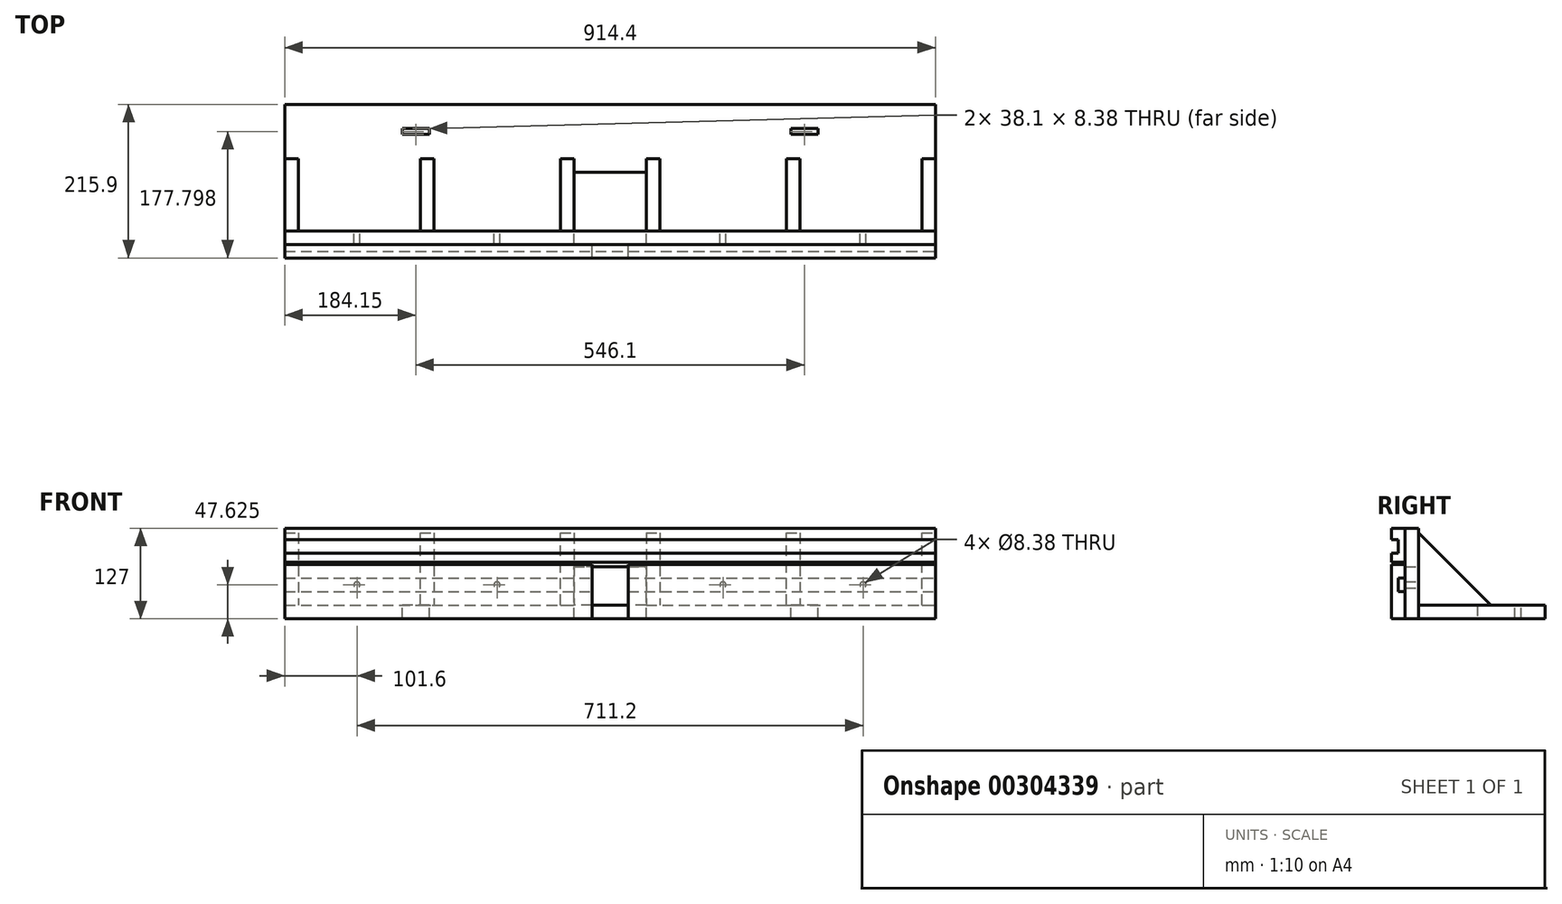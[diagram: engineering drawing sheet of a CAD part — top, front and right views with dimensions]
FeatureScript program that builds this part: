
annotation { "Feature Type Name" : "Feature", "Feature Type Description" : "" }
export const myFeature = defineFeature(function(context is Context, id is Id, definition is map)
    precondition{}
    {
        {
            var Q0;
            Q0=qCreatedBy(makeId("Top.planeOp"),FACE);
            var sketch = newSketch(context, id + "F0", { "sketchPlane" : qUnion([Q0])});
            skLineSegment(sketch, "E0.bottom", {"start": v(-457.2, 69.56) * mm, "end": v(457.2, 69.56) * mm});
            skLineSegment(sketch, "E0.top", {"start": v(-457.2, -108.24) * mm, "end": v(457.2, -108.24) * mm});
            skLineSegment(sketch, "E0.left", {"start": v(-457.2, 69.56) * mm, "end": v(-457.2, -108.24) * mm});
            skLineSegment(sketch, "E0.right", {"start": v(457.2, 69.56) * mm, "end": v(457.2, -108.24) * mm});
            skPoint(sketch, "E1", {"position": v(0, 69.56) * mm});
            skSolve(sketch);
        }
        {
            var Q0;
            Q0=makeQuery(id+"F0.imprint","IMPRINT",FACE,{"disambiguationData":[TD([[makeQuery(id+"F0.imprint","IMPRINT",EDGE,{"derivedFrom":sQuery(id+"F0.wireOp",EDGE,"E0.bottom")}),-1.0]])]});
            extrude(context, id + "F1", {"entities" : qUnion([Q0]), "depth" : 19.05 * mm});
        }
        {
            var Q0;
            Q0=makeQuery(id+"F1.opExtrude","CAP_FACE",FACE,{"disambiguationData":[OSD([sQuery(id+"F0.wireOp",EDGE,"E0.bottom"),sQuery(id+"F0.wireOp",EDGE,"E0.top"),sQuery(id+"F0.wireOp",EDGE,"E0.left"),sQuery(id+"F0.wireOp",EDGE,"E0.right")])],"isStart":true});
            var sketch = newSketch(context, id + "F2", { "sketchPlane" : qUnion([Q0])});
            skLineSegment(sketch, "E2.bottom", {"start": v(-457.2, 108.24) * mm, "end": v(457.2, 108.24) * mm});
            skLineSegment(sketch, "E2.top", {"start": v(-457.2, 127.3) * mm, "end": v(457.2, 127.3) * mm});
            skLineSegment(sketch, "E2.left", {"start": v(-457.2, 108.24) * mm, "end": v(-457.2, 127.3) * mm});
            skLineSegment(sketch, "E2.right", {"start": v(457.2, 108.24) * mm, "end": v(457.2, 127.3) * mm});
            skSolve(sketch);
        }
        {
            var Q0;
            Q0=makeQuery(id+"F2.imprint","IMPRINT",FACE,{"disambiguationData":[TD([[makeQuery(id+"F2.imprint","IMPRINT",EDGE,{"derivedFrom":sQuery(id+"F2.wireOp",EDGE,"E2.bottom")}),1.0]])]});
            extrude(context, id + "F3", {"entities" : qUnion([Q0]), "oppositeDirection" : true, "depth" : 127 * mm});
        }
        {
            var Q0;
            Q0=makeQuery(id+"F3.opExtrude","SWEPT_FACE",FACE,{"disambiguationData":[OSD([sQuery(id+"F2.wireOp",EDGE,"E2.top")])]});
            var sketch = newSketch(context, id + "F4", { "sketchPlane" : qUnion([Q0])});
            skLineSegment(sketch, "E3.bottom", {"start": v(-457.2, 0) * mm, "end": v(-25.4, 0) * mm});
            skLineSegment(sketch, "E3.top", {"start": v(-457.2, 76.2) * mm, "end": v(-25.4, 76.2) * mm});
            skLineSegment(sketch, "E3.left", {"start": v(-457.2, 0) * mm, "end": v(-457.2, 76.2) * mm});
            skLineSegment(sketch, "E3.right", {"start": v(-25.4, 0) * mm, "end": v(-25.4, 76.2) * mm});
            skLineSegment(sketch, "E4.bottom", {"start": v(457.2, 0) * mm, "end": v(25.4, 0) * mm});
            skLineSegment(sketch, "E4.top", {"start": v(457.2, 76.2) * mm, "end": v(25.4, 76.2) * mm});
            skLineSegment(sketch, "E4.left", {"start": v(457.2, 0) * mm, "end": v(457.2, 76.2) * mm});
            skLineSegment(sketch, "E4.right", {"start": v(25.4, 0) * mm, "end": v(25.4, 76.2) * mm});
            skSolve(sketch);
        }
        {
            var Q0;
            Q0=makeQuery(id+"F4.imprint","IMPRINT",FACE,{"disambiguationData":[TD([[makeQuery(id+"F4.imprint","IMPRINT",EDGE,{"derivedFrom":sQuery(id+"F4.wireOp",EDGE,"E3.bottom")}),1.0]])]});
            var Q1;
            Q1=makeQuery(id+"F4.imprint","IMPRINT",FACE,{"disambiguationData":[TD([[makeQuery(id+"F4.imprint","IMPRINT",EDGE,{"derivedFrom":sQuery(id+"F4.wireOp",EDGE,"E4.bottom")}),1.0]])]});
            extrude(context, id + "F5", {"entities" : qUnion([Q0, Q1]), "depth" : 19.05 * mm});
        }
        {
            var Q0;
            Q0=makeQuery(id+"F3.opExtrude","SWEPT_FACE",FACE,{"disambiguationData":[OSD([sQuery(id+"F2.wireOp",EDGE,"E2.top")])]});
            var sketch = newSketch(context, id + "F6", { "sketchPlane" : qUnion([Q0])});
            skLineSegment(sketch, "E5.bottom", {"start": v(-457.2, 127) * mm, "end": v(457.2, 127) * mm});
            skLineSegment(sketch, "E5.top", {"start": v(-457.2, 79.25) * mm, "end": v(457.2, 79.25) * mm});
            skLineSegment(sketch, "E5.left", {"start": v(-457.2, 127) * mm, "end": v(-457.2, 79.25) * mm});
            skLineSegment(sketch, "E5.right", {"start": v(457.2, 127) * mm, "end": v(457.2, 79.25) * mm});
            skSolve(sketch);
        }
        {
            var Q0;
            Q0=makeQuery(id+"F6.imprint","IMPRINT",FACE,{"disambiguationData":[TD([[makeQuery(id+"F6.imprint","IMPRINT",EDGE,{"derivedFrom":sQuery(id+"F6.wireOp",EDGE,"E5.bottom")}),-1.0]])]});
            extrude(context, id + "F7", {"entities" : qUnion([Q0]), "depth" : 19.05 * mm});
        }
        {
            var Q0;
            Q0=makeQuery(id+"F7.opExtrude","SWEPT_FACE",FACE,{"disambiguationData":[OSD([sQuery(id+"F6.wireOp",EDGE,"E5.right")])]});
            var sketch = newSketch(context, id + "F8", { "sketchPlane" : qUnion([Q0])});
            skLineSegment(sketch, "E6.bottom", {"start": v(-146.34, 111) * mm, "end": v(-136.82, 111) * mm});
            skLineSegment(sketch, "E6.top", {"start": v(-146.34, 91.95) * mm, "end": v(-136.82, 91.95) * mm});
            skLineSegment(sketch, "E6.left", {"start": v(-146.34, 111) * mm, "end": v(-146.34, 91.95) * mm});
            skLineSegment(sketch, "E6.right", {"start": v(-136.82, 111) * mm, "end": v(-136.82, 91.95) * mm});
            skSolve(sketch);
        }
        {
            var Q0;
            Q0=makeQuery(id+"F8.imprint","IMPRINT",FACE,{"disambiguationData":[TD([[makeQuery(id+"F8.imprint","IMPRINT",EDGE,{"derivedFrom":sQuery(id+"F8.wireOp",EDGE,"E6.bottom")}),-1.0]])]});
            var Q1;
            Q1=makeQuery(id+"F7.opExtrude","SWEPT_FACE",FACE,{"disambiguationData":[OSD([sQuery(id+"F6.wireOp",EDGE,"E5.left")])]});
            extrude(context, id + "F9", {"entities" : qUnion([Q0]), "operationType" : NewBodyOperationType.REMOVE, "endBound" : BoundingType.UP_TO_SURFACE, "oppositeDirection" : true, "endBoundEntityFace" : qUnion([Q1]), "depth" : 25.4 * mm});
        }
        {
            var Q0;
            Q0=makeQuery(id+"F1.opExtrude","CAP_FACE",FACE,{"disambiguationData":[OSD([sQuery(id+"F0.wireOp",EDGE,"E0.bottom"),sQuery(id+"F0.wireOp",EDGE,"E0.top"),sQuery(id+"F0.wireOp",EDGE,"E0.left"),sQuery(id+"F0.wireOp",EDGE,"E0.right")])],"isStart":false});
            var sketch = newSketch(context, id + "F10", { "sketchPlane" : qUnion([Q0])});
            skLineSegment(sketch, "E7.bottom", {"start": v(-457.2, -108.24) * mm, "end": v(-438.15, -108.24) * mm});
            skLineSegment(sketch, "E7.top", {"start": v(-457.2, -6.64) * mm, "end": v(-438.15, -6.64) * mm});
            skLineSegment(sketch, "E7.left", {"start": v(-457.2, -108.24) * mm, "end": v(-457.2, -6.64) * mm});
            skLineSegment(sketch, "E7.right", {"start": v(-438.15, -108.24) * mm, "end": v(-438.15, -6.64) * mm});
            skLineSegment(sketch, "E8.bottom", {"start": v(-69.85, -108.24) * mm, "end": v(-50.8, -108.24) * mm});
            skLineSegment(sketch, "E8.top", {"start": v(-69.85, -6.64) * mm, "end": v(-50.8, -6.64) * mm});
            skLineSegment(sketch, "E8.left", {"start": v(-69.85, -108.24) * mm, "end": v(-69.85, -6.64) * mm});
            skLineSegment(sketch, "E8.right", {"start": v(-50.8, -108.24) * mm, "end": v(-50.8, -6.64) * mm});
            skLineSegment(sketch, "E9.bottom", {"start": v(50.8, -108.24) * mm, "end": v(69.85, -108.24) * mm});
            skLineSegment(sketch, "E9.top", {"start": v(50.8, -6.64) * mm, "end": v(69.85, -6.64) * mm});
            skLineSegment(sketch, "E9.left", {"start": v(50.8, -108.24) * mm, "end": v(50.8, -6.64) * mm});
            skLineSegment(sketch, "E9.right", {"start": v(69.85, -108.24) * mm, "end": v(69.85, -6.64) * mm});
            skLineSegment(sketch, "E10.bottom", {"start": v(457.2, -108.24) * mm, "end": v(438.15, -108.24) * mm});
            skLineSegment(sketch, "E10.top", {"start": v(457.2, -6.64) * mm, "end": v(438.15, -6.64) * mm});
            skLineSegment(sketch, "E10.left", {"start": v(457.2, -108.24) * mm, "end": v(457.2, -6.64) * mm});
            skLineSegment(sketch, "E10.right", {"start": v(438.15, -108.24) * mm, "end": v(438.15, -6.64) * mm});
            skLineSegment(sketch, "E11.bottom", {"start": v(-266.7, -108.24) * mm, "end": v(-247.65, -108.24) * mm});
            skLineSegment(sketch, "E11.top", {"start": v(-266.7, -6.64) * mm, "end": v(-247.65, -6.64) * mm});
            skLineSegment(sketch, "E11.left", {"start": v(-266.7, -108.24) * mm, "end": v(-266.7, -6.64) * mm});
            skLineSegment(sketch, "E11.right", {"start": v(-247.65, -108.24) * mm, "end": v(-247.65, -6.64) * mm});
            skLineSegment(sketch, "E12.bottom", {"start": v(247.65, -108.24) * mm, "end": v(266.7, -108.24) * mm});
            skLineSegment(sketch, "E12.left", {"start": v(247.65, -108.24) * mm, "end": v(247.65, -6.64) * mm});
            skLineSegment(sketch, "E12.right", {"start": v(266.7, -108.24) * mm, "end": v(266.7, -6.64) * mm});
            skLineSegment(sketch, "E13", {"start": v(266.7, -6.64) * mm, "end": v(247.65, -6.64) * mm});
            skSolve(sketch);
        }
        {
            var Q0;
            Q0=makeQuery(id+"F10.imprint","IMPRINT",FACE,{"disambiguationData":[TD([[makeQuery(id+"F10.imprint","IMPRINT",EDGE,{"derivedFrom":sQuery(id+"F10.wireOp",EDGE,"E7.bottom")}),1.0]])]});
            var Q1;
            Q1=makeQuery(id+"F10.imprint","IMPRINT",FACE,{"disambiguationData":[TD([[makeQuery(id+"F10.imprint","IMPRINT",EDGE,{"derivedFrom":sQuery(id+"F10.wireOp",EDGE,"E11.bottom")}),1.0]])]});
            var Q2;
            Q2=makeQuery(id+"F10.imprint","IMPRINT",FACE,{"disambiguationData":[TD([[makeQuery(id+"F10.imprint","IMPRINT",EDGE,{"derivedFrom":sQuery(id+"F10.wireOp",EDGE,"E8.bottom")}),1.0]])]});
            var Q3;
            Q3=makeQuery(id+"F10.imprint","IMPRINT",FACE,{"disambiguationData":[TD([[makeQuery(id+"F10.imprint","IMPRINT",EDGE,{"derivedFrom":sQuery(id+"F10.wireOp",EDGE,"E9.bottom")}),1.0]])]});
            var Q4;
            Q4=makeQuery(id+"F10.imprint","IMPRINT",FACE,{"disambiguationData":[TD([[makeQuery(id+"F10.imprint","IMPRINT",EDGE,{"derivedFrom":sQuery(id+"F10.wireOp",EDGE,"E12.bottom")}),1.0]])]});
            var Q5;
            Q5=makeQuery(id+"F10.imprint","IMPRINT",FACE,{"disambiguationData":[TD([[makeQuery(id+"F10.imprint","IMPRINT",EDGE,{"derivedFrom":sQuery(id+"F10.wireOp",EDGE,"E10.bottom")}),1.0]])]});
            extrude(context, id + "F11", {"entities" : qUnion([Q0, Q1, Q2, Q3, Q4, Q5]), "depth" : 101.6 * mm});
        }
        {
            var Q0;
            Q0=makeQuery(id+"F11.opExtrude","SWEPT_FACE",FACE,{"disambiguationData":[OSD([sQuery(id+"F10.wireOp",EDGE,"E7.left")])]});
            var sketch = newSketch(context, id + "F12", { "sketchPlane" : qUnion([Q0])});
            skLineSegment(sketch, "E14", {"start": v(6.64, 19.05) * mm, "end": v(108.24, 120.65) * mm});
            skLineSegment(sketch, "E15", {"start": v(108.24, 120.65) * mm, "end": v(6.64, 120.65) * mm});
            skLineSegment(sketch, "E16", {"start": v(6.64, 120.65) * mm, "end": v(6.64, 19.05) * mm});
            skSolve(sketch);
        }
        {
            var Q0;
            Q0=makeQuery(id+"F12.imprint","IMPRINT",FACE,{"disambiguationData":[TD([[makeQuery(id+"F12.imprint","IMPRINT",EDGE,{"derivedFrom":sQuery(id+"F12.wireOp",EDGE,"E14")}),1.0]])]});
            var Q1;
            Q1=makeQuery(id+"F11.opExtrude","SWEPT_FACE",FACE,{"disambiguationData":[OSD([sQuery(id+"F10.wireOp",EDGE,"E10.left")])]});
            extrude(context, id + "F13", {"entities" : qUnion([Q0]), "operationType" : NewBodyOperationType.REMOVE, "endBound" : BoundingType.UP_TO_SURFACE, "oppositeDirection" : true, "endBoundEntityFace" : qUnion([Q1]), "depth" : 25.4 * mm});
        }
        {
            var Q0;
            Q0=makeQuery(id+"F3.opExtrude","CAP_FACE",FACE,{"disambiguationData":[OSD([sQuery(id+"F2.wireOp",EDGE,"E2.bottom"),sQuery(id+"F2.wireOp",EDGE,"E2.top"),sQuery(id+"F2.wireOp",EDGE,"E2.left"),sQuery(id+"F2.wireOp",EDGE,"E2.right")])],"isStart":true});
            var sketch = newSketch(context, id + "F14", { "sketchPlane" : qUnion([Q0])});
            skLineSegment(sketch, "E17.bottom", {"start": v(-50.8, 127.3) * mm, "end": v(50.8, 127.3) * mm});
            skLineSegment(sketch, "E17.top", {"start": v(-50.8, 25.7) * mm, "end": v(50.8, 25.7) * mm});
            skLineSegment(sketch, "E17.left", {"start": v(-50.8, 127.3) * mm, "end": v(-50.8, 25.7) * mm});
            skLineSegment(sketch, "E17.right", {"start": v(50.8, 127.3) * mm, "end": v(50.8, 25.7) * mm});
            skPoint(sketch, "E18", {"position": v(0, 25.7) * mm});
            skSolve(sketch);
        }
        {
            var Q0;
            {var subQ0=sQuery(id+"F14.wireOp",EDGE,"E17.top");Q0=makeQuery(id+"F14.imprint","IMPRINT",FACE,{"disambiguationData":[TD([[makeQuery(id+"F14.imprint","IMPRINT",EDGE,{"derivedFrom":subQ0}),1.0]])]});}
            var Q1;
            {var subQ0=sQuery(id+"F14.wireOp",EDGE,"E17.bottom");Q1=makeQuery(id+"F14.imprint","IMPRINT",FACE,{"disambiguationData":[TD([[makeQuery(id+"F14.imprint","IMPRINT",EDGE,{"derivedFrom":subQ0}),-1.0]])]});}
            extrude(context, id + "F15", {"entities" : qUnion([Q0, Q1]), "operationType" : NewBodyOperationType.REMOVE, "oppositeDirection" : true, "depth" : 73.15 * mm});
        }
        {
            var Q0;
            Q0=makeQuery(id+"F5.opExtrude","SWEPT_FACE",FACE,{"disambiguationData":[OSD([sQuery(id+"F4.wireOp",EDGE,"E4.left")])]});
            var sketch = newSketch(context, id + "F16", { "sketchPlane" : qUnion([Q0])});
            skLineSegment(sketch, "E19.bottom", {"start": v(-127.3, 57.15) * mm, "end": v(-136.82, 57.15) * mm});
            skLineSegment(sketch, "E19.top", {"start": v(-127.3, 38.1) * mm, "end": v(-136.82, 38.1) * mm});
            skLineSegment(sketch, "E19.left", {"start": v(-127.3, 57.15) * mm, "end": v(-127.3, 38.1) * mm});
            skLineSegment(sketch, "E19.right", {"start": v(-136.82, 57.15) * mm, "end": v(-136.82, 38.1) * mm});
            skSolve(sketch);
        }
        {
            var Q0;
            Q0=makeQuery(id+"F16.imprint","IMPRINT",FACE,{"disambiguationData":[TD([[makeQuery(id+"F16.imprint","IMPRINT",EDGE,{"derivedFrom":sQuery(id+"F16.wireOp",EDGE,"E19.bottom")}),1.0]])]});
            var Q1;
            Q1=makeQuery(id+"F5.opExtrude","SWEPT_FACE",FACE,{"disambiguationData":[OSD([sQuery(id+"F4.wireOp",EDGE,"E3.left")])]});
            extrude(context, id + "F17", {"entities" : qUnion([Q0]), "operationType" : NewBodyOperationType.REMOVE, "endBound" : BoundingType.UP_TO_SURFACE, "oppositeDirection" : true, "endBoundEntityFace" : qUnion([Q1]), "depth" : 25.4 * mm});
        }
        {
            var Q0;
            Q0=makeQuery(id+"F3.opExtrude","SWEPT_FACE",FACE,{"disambiguationData":[OSD([sQuery(id+"F2.wireOp",EDGE,"E2.bottom")])]});
            var sketch = newSketch(context, id + "F18", { "sketchPlane" : qUnion([Q0])});
            skCircle(sketch, "E20", {"center": v(-355.6, 47.62) * mm, "radius": 4.2 * mm});
            skCircle(sketch, "E21", {"center": v(158.75, 47.62) * mm, "radius": 4.2 * mm});
            skCircle(sketch, "E22", {"center": v(355.6, 47.62) * mm, "radius": 4.2 * mm});
            skCircle(sketch, "E23", {"center": v(-158.75, 47.62) * mm, "radius": 4.2 * mm});
            skSolve(sketch);
        }
        {
            var Q0;
            Q0=makeQuery(id+"F18.imprint","IMPRINT",FACE,{"disambiguationData":[TD([[makeQuery(id+"F18.imprint","IMPRINT",EDGE,{"derivedFrom":sQuery(id+"F18.wireOp",EDGE,"E20")}),1.0]])]});
            var Q1;
            Q1=makeQuery(id+"F18.imprint","IMPRINT",FACE,{"disambiguationData":[TD([[makeQuery(id+"F18.imprint","IMPRINT",EDGE,{"derivedFrom":sQuery(id+"F18.wireOp",EDGE,"eWh7vWQh-USRD-DjUJ-84Nm-SUygQDbZihJi")}),1.0]])]});
            var Q2;
            Q2=makeQuery(id+"F18.imprint","IMPRINT",FACE,{"disambiguationData":[TD([[makeQuery(id+"F18.imprint","IMPRINT",EDGE,{"derivedFrom":sQuery(id+"F18.wireOp",EDGE,"E21")}),1.0]])]});
            var Q3;
            Q3=makeQuery(id+"F18.imprint","IMPRINT",FACE,{"disambiguationData":[TD([[makeQuery(id+"F18.imprint","IMPRINT",EDGE,{"derivedFrom":sQuery(id+"F18.wireOp",EDGE,"E22")}),1.0]])]});
            var Q4;
            Q4=makeQuery(id+"F18.imprint","IMPRINT",FACE,{"disambiguationData":[TD([[makeQuery(id+"F18.imprint","IMPRINT",EDGE,{"derivedFrom":sQuery(id+"F18.wireOp",EDGE,"E23")}),1.0]])]});
            extrude(context, id + "F19", {"entities" : qUnion([Q0, Q1, Q2, Q3, Q4]), "operationType" : NewBodyOperationType.REMOVE, "oppositeDirection" : true, "depth" : 19.05 * mm});
        }
        {
            var Q0;
            Q0=makeQuery(id+"F1.opExtrude","CAP_FACE",FACE,{"disambiguationData":[OSD([sQuery(id+"F0.wireOp",EDGE,"E0.bottom"),sQuery(id+"F0.wireOp",EDGE,"E0.top"),sQuery(id+"F0.wireOp",EDGE,"E0.left"),sQuery(id+"F0.wireOp",EDGE,"E0.right")])],"isStart":false});
            var sketch = newSketch(context, id + "F20", { "sketchPlane" : qUnion([Q0])});
            skLineSegment(sketch, "E24.bottom", {"start": v(-273.05, 118.73) * mm, "end": v(273.05, 118.73) * mm});
            skLineSegment(sketch, "E24.left", {"start": v(-273.05, 118.73) * mm, "end": v(-273.05, 31.46) * mm});
            skLineSegment(sketch, "E24.right", {"start": v(273.05, 118.73) * mm, "end": v(273.05, 31.46) * mm});
            skPoint(sketch, "E25", {"position": v(0, 118.73) * mm});
            skLineSegment(sketch, "E26.bottom", {"start": v(-254, 27.27) * mm, "end": v(-292.1, 27.27) * mm});
            skLineSegment(sketch, "E26.top", {"start": v(-254, 35.65) * mm, "end": v(-292.1, 35.65) * mm});
            skLineSegment(sketch, "E26.left", {"start": v(-254, 27.27) * mm, "end": v(-254, 35.65) * mm});
            skLineSegment(sketch, "E26.right", {"start": v(-292.1, 27.27) * mm, "end": v(-292.1, 35.65) * mm});
            skPoint(sketch, "E26.middle", {"position": v(-273.05, 31.46) * mm});
            skLineSegment(sketch, "E27.bottom", {"start": v(292.1, 27.27) * mm, "end": v(254, 27.27) * mm});
            skLineSegment(sketch, "E27.top", {"start": v(292.1, 35.65) * mm, "end": v(254, 35.65) * mm});
            skLineSegment(sketch, "E27.left", {"start": v(292.1, 27.27) * mm, "end": v(292.1, 35.65) * mm});
            skLineSegment(sketch, "E27.right", {"start": v(254, 27.27) * mm, "end": v(254, 35.65) * mm});
            skPoint(sketch, "E27.middle", {"position": v(273.05, 31.46) * mm});
            skSolve(sketch);
        }
        {
            var Q0;
            Q0=makeQuery(id+"F20.imprint","IMPRINT",FACE,{"disambiguationData":[TD([[makeQuery(id+"F20.imprint","IMPRINT",EDGE,{"derivedFrom":sQuery(id+"F20.wireOp",EDGE,"E26.bottom")}),-1.0]])]});
            var Q1;
            Q1=makeQuery(id+"F20.imprint","IMPRINT",FACE,{"disambiguationData":[TD([[makeQuery(id+"F20.imprint","IMPRINT",EDGE,{"derivedFrom":sQuery(id+"F20.wireOp",EDGE,"E27.bottom")}),-1.0]])]});
            var Q2;
            Q2=makeQuery(id+"F1.opExtrude","CAP_FACE",FACE,{"disambiguationData":[OSD([sQuery(id+"F0.wireOp",EDGE,"E0.bottom"),sQuery(id+"F0.wireOp",EDGE,"E0.top"),sQuery(id+"F0.wireOp",EDGE,"E0.left"),sQuery(id+"F0.wireOp",EDGE,"E0.right")])],"isStart":true});
            extrude(context, id + "F21", {"entities" : qUnion([Q0, Q1]), "operationType" : NewBodyOperationType.REMOVE, "endBound" : BoundingType.UP_TO_SURFACE, "oppositeDirection" : true, "endBoundEntityFace" : qUnion([Q2]), "depth" : 25.4 * mm});
        }
    });
